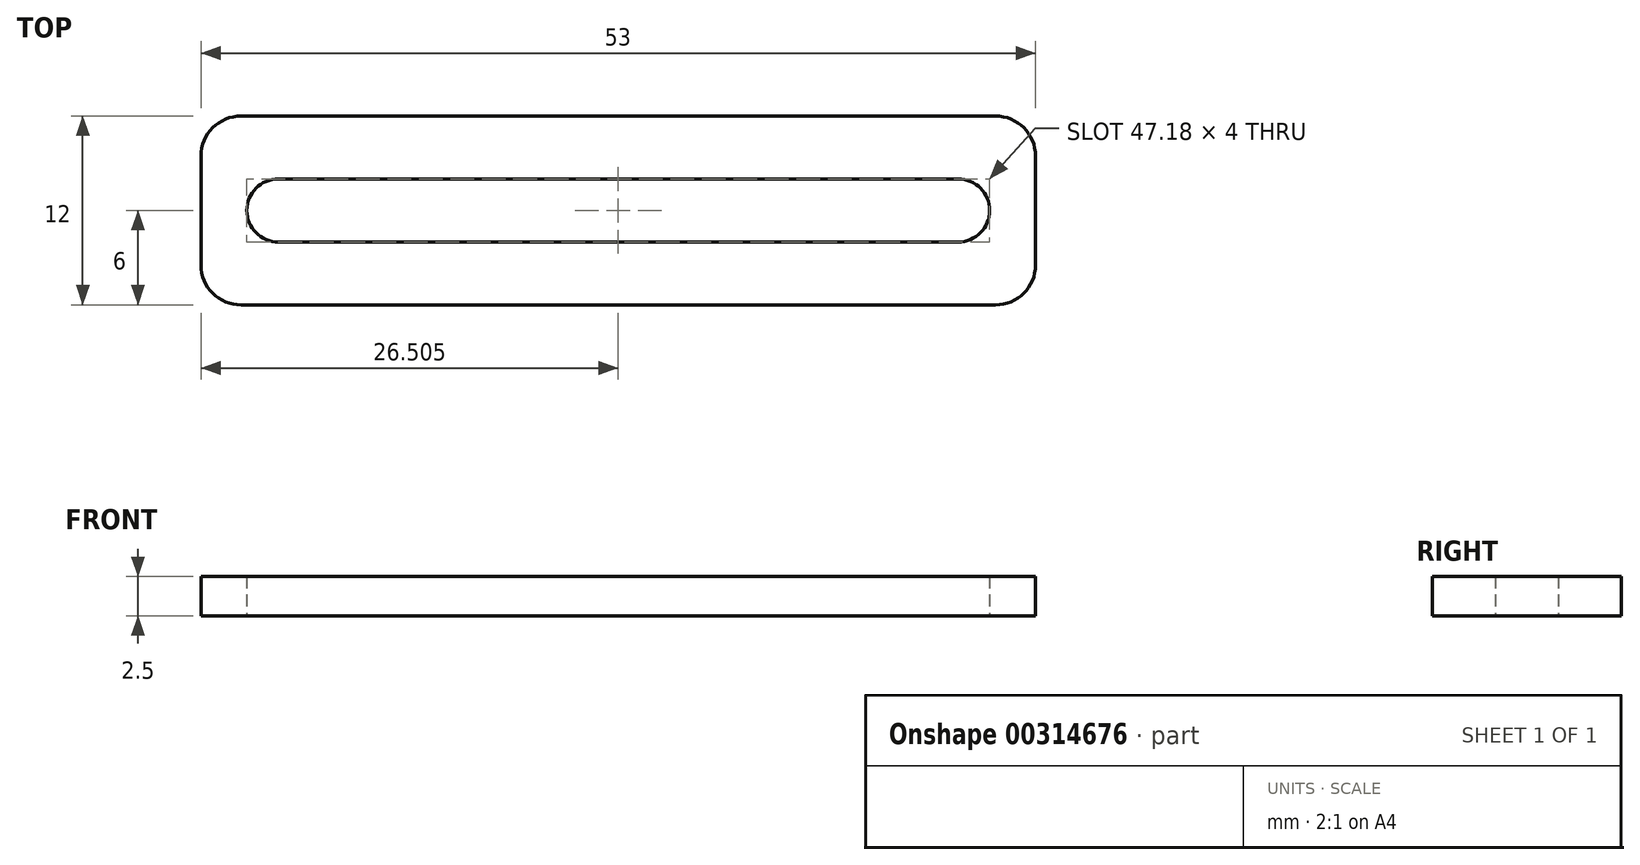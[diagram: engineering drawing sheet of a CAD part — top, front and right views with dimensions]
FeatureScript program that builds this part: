
annotation { "Feature Type Name" : "Feature", "Feature Type Description" : "" }
export const myFeature = defineFeature(function(context is Context, id is Id, definition is map)
    precondition{}
    {
        {
            var Q0;
            Q0=qCreatedBy(makeId("Top.planeOp"),FACE);
            var sketch = newSketch(context, id + "F0", { "sketchPlane" : qUnion([Q0])});
            skLineSegment(sketch, "E0.bottom", {"start": v(-58.93, 24.9) * mm, "end": v(-5.93, 24.9) * mm});
            skLineSegment(sketch, "E0.top", {"start": v(-58.93, 12.9) * mm, "end": v(-5.93, 12.9) * mm});
            skLineSegment(sketch, "E0.left", {"start": v(-58.93, 24.9) * mm, "end": v(-58.93, 12.9) * mm});
            skLineSegment(sketch, "E0.right", {"start": v(-5.93, 24.9) * mm, "end": v(-5.93, 12.9) * mm});
            skPoint(sketch, "E0.middle", {"position": v(-32.43, 18.9) * mm});
            skLineSegment(sketch, "E1", {"start": v(-10.84, 18.9) * mm, "end": v(-54.02, 18.9) * mm, "construction": true});
            skArc(sketch, "E2.0.startCap", {"start": v(-10.84, 20.9) * mm, "mid": v(-8.84, 18.9) * mm, "end": v(-10.84, 16.9) * mm});
            skArc(sketch, "E2.0.endCap", {"start": v(-54.02, 16.9) * mm, "mid": v(-56.02, 18.9) * mm, "end": v(-54.02, 20.9) * mm});
            skLineSegment(sketch, "E2.0.left", {"start": v(-10.84, 16.9) * mm, "end": v(-54.02, 16.9) * mm});
            skLineSegment(sketch, "E2.0.right", {"start": v(-10.84, 20.9) * mm, "end": v(-54.02, 20.9) * mm});
            skSolve(sketch);
        }
        {
            var Q0;
            Q0 = qSketchRegion(id + "F0", true);
            extrude(context, id + "F1", {"entities" : qUnion([Q0]), "depth" : 2.5 * mm});
        }
        {
            var Q0;
            Q0=makeQuery(id+"F1.opExtrude","SWEPT_EDGE",EDGE,{"disambiguationData":[OSD([sQuery(id+"F0.wireOp",EDGE,"E0.bottom"),sQuery(id+"F0.wireOp",EDGE,"E0.left")])]});
            var Q1;
            Q1=makeQuery(id+"F1.opExtrude","SWEPT_EDGE",EDGE,{"disambiguationData":[OSD([sQuery(id+"F0.wireOp",EDGE,"E0.top"),sQuery(id+"F0.wireOp",EDGE,"E0.left")])]});
            var Q2;
            Q2=makeQuery(id+"F1.opExtrude","SWEPT_EDGE",EDGE,{"disambiguationData":[OSD([sQuery(id+"F0.wireOp",EDGE,"E0.top"),sQuery(id+"F0.wireOp",EDGE,"E0.right")])]});
            var Q3;
            Q3=makeQuery(id+"F1.opExtrude","SWEPT_EDGE",EDGE,{"disambiguationData":[OSD([sQuery(id+"F0.wireOp",EDGE,"E0.bottom"),sQuery(id+"F0.wireOp",EDGE,"E0.right")])]});
            fillet(context, id + "F2", {"entities" : qUnion([Q0, Q1, Q2, Q3]), "radius" : 2.54 * mm, "tangentPropagation" : true, "allowEdgeOverflow" : false});
        }
    });
